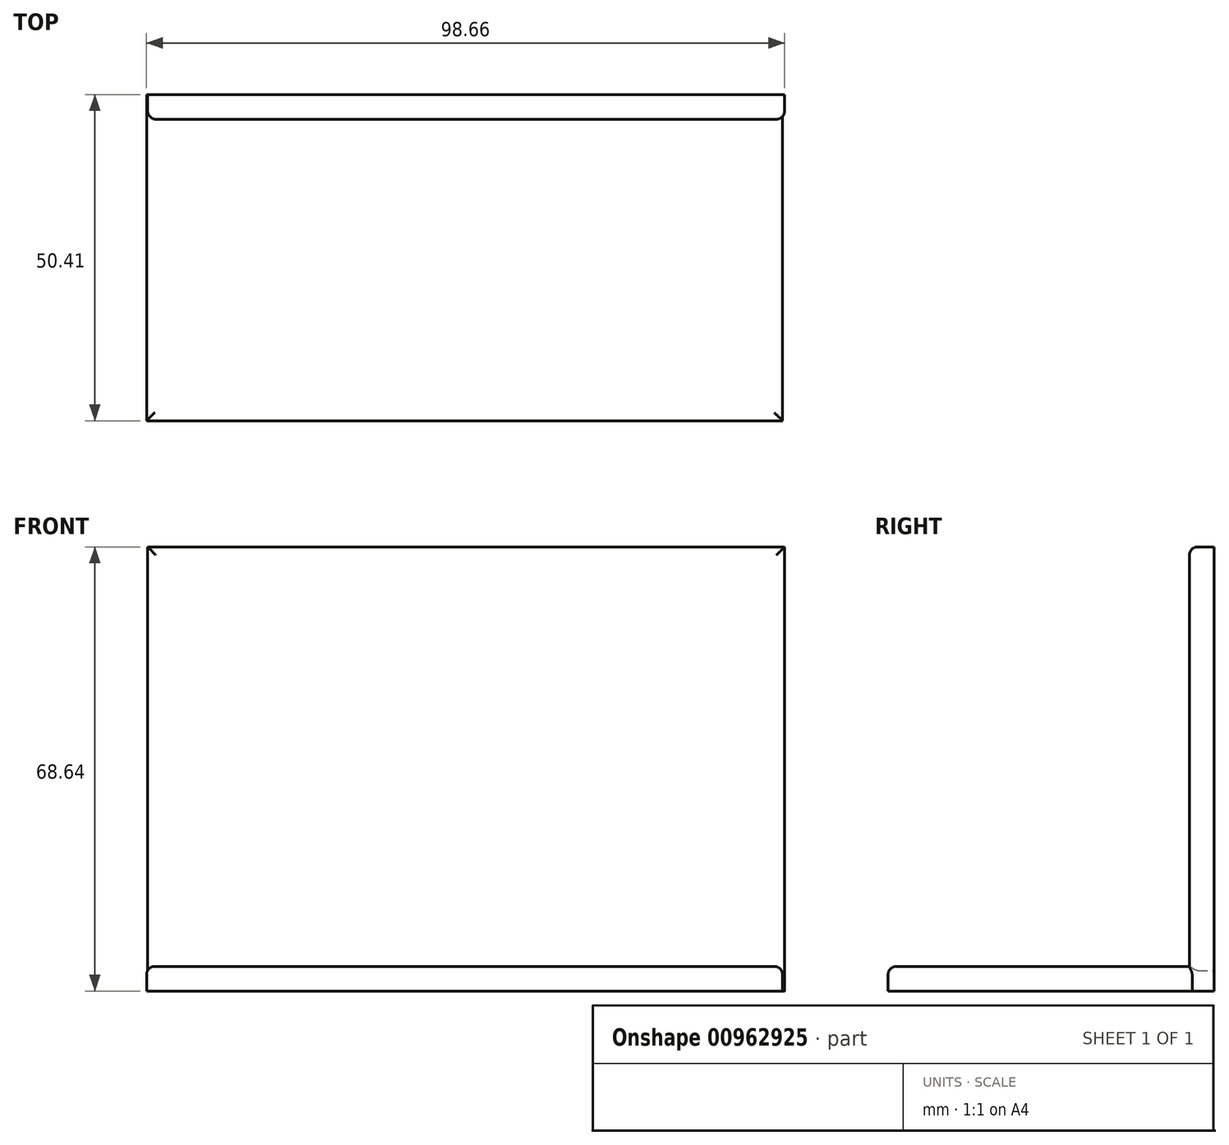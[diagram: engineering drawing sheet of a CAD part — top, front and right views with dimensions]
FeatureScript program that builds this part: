
annotation { "Feature Type Name" : "Feature", "Feature Type Description" : "" }
export const myFeature = defineFeature(function(context is Context, id is Id, definition is map)
    precondition{}
    {
        {
            var Q0;
            Q0=qCreatedBy(makeId("Top.planeOp"),FACE);
            var sketch = newSketch(context, id + "F0", { "sketchPlane" : qUnion([Q0])});
            skLineSegment(sketch, "E0.bottom", {"start": v(-46.6, -50.4) * mm, "end": v(51.74, -50.4) * mm});
            skLineSegment(sketch, "E0.top", {"start": v(-46.6, 0) * mm, "end": v(51.74, 0) * mm});
            skLineSegment(sketch, "E0.left", {"start": v(-46.6, -50.4) * mm, "end": v(-46.6, 0) * mm});
            skLineSegment(sketch, "E0.right", {"start": v(51.74, -50.4) * mm, "end": v(51.74, 0) * mm});
            skSolve(sketch);
        }
        {
            var Q0;
            Q0=qCreatedBy(makeId("Front.planeOp"),FACE);
            var sketch = newSketch(context, id + "F1", { "sketchPlane" : qUnion([Q0])});
            skLineSegment(sketch, "E1.bottom", {"start": v(-46.43, 0) * mm, "end": v(52.06, 0) * mm});
            skLineSegment(sketch, "E1.top", {"start": v(-46.43, 68.64) * mm, "end": v(52.06, 68.64) * mm});
            skLineSegment(sketch, "E1.left", {"start": v(-46.43, 0) * mm, "end": v(-46.43, 68.64) * mm});
            skLineSegment(sketch, "E1.right", {"start": v(52.06, 0) * mm, "end": v(52.06, 68.64) * mm});
            skSolve(sketch);
        }
        {
            var Q0;
            Q0=makeQuery(id+"F1.imprint","IMPRINT",FACE,{"disambiguationData":[TD([[makeQuery(id+"F1.imprint","IMPRINT",EDGE,{"derivedFrom":sQuery(id+"F1.wireOp",EDGE,"E1.bottom")}),1.0]])]});
            extrude(context, id + "F2", {"entities" : qUnion([Q0]), "depth" : 3.8 * mm, "offsetDistance" : 25.4 * mm});
        }
        {
            var Q0;
            Q0=makeQuery(id+"F0.imprint","IMPRINT",FACE,{"disambiguationData":[TD([[makeQuery(id+"F0.imprint","IMPRINT",EDGE,{"derivedFrom":sQuery(id+"F0.wireOp",EDGE,"E0.bottom")}),1.0]])]});
            extrude(context, id + "F3", {"entities" : qUnion([Q0]), "operationType" : NewBodyOperationType.ADD, "depth" : 3.8 * mm, "offsetDistance" : 25.4 * mm});
        }
        {
            var Q0;
            Q0=makeQuery(id+"F2.opExtrude","CAP_EDGE",EDGE,{"disambiguationData":[OSD([sQuery(id+"F1.wireOp",EDGE,"E1.left")])],"isStart":false});
            var Q1;
            Q1=makeQuery(id+"F2.opExtrude","CAP_EDGE",EDGE,{"disambiguationData":[OSD([sQuery(id+"F1.wireOp",EDGE,"E1.top")])],"isStart":false});
            var Q2;
            Q2=makeQuery(id+"F2.opExtrude","CAP_EDGE",EDGE,{"disambiguationData":[OSD([sQuery(id+"F1.wireOp",EDGE,"E1.right")])],"isStart":false});
            fillet(context, id + "F4", {"entities" : qUnion([Q0, Q1, Q2]), "radius" : 1.27 * mm, "tangentPropagation" : true, "allowEdgeOverflow" : false});
        }
        {
            var Q0;
            Q0=makeQuery(id+"F3.opExtrude","CAP_EDGE",EDGE,{"disambiguationData":[OSD([sQuery(id+"F0.wireOp",EDGE,"E0.bottom")])],"isStart":false});
            var Q1;
            Q1=makeQuery(id+"F3.opExtrude","CAP_EDGE",EDGE,{"disambiguationData":[OSD([sQuery(id+"F0.wireOp",EDGE,"E0.right")])],"isStart":false});
            var Q2;
            Q2=makeQuery(id+"F3.opExtrude","CAP_EDGE",EDGE,{"disambiguationData":[OSD([sQuery(id+"F0.wireOp",EDGE,"E0.left")])],"isStart":false});
            fillet(context, id + "F5", {"entities" : qUnion([Q0, Q1, Q2]), "radius" : 1.27 * mm, "tangentPropagation" : true, "allowEdgeOverflow" : false});
        }
    });
